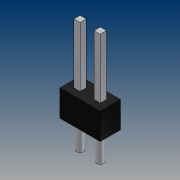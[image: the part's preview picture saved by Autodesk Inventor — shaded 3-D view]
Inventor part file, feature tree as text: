
AUTODESK INVENTOR PART (.ipt)
format: ipt  version: 2012 (Build 160160000, 160)  size: 101,376 bytes
history: native  units: mm (DEFAULTED — no unit token found)
features: extrude x3, plane x3, sketch x2, pattern_linear x1
ambient origin geometry x5: Origin, X Axis, Y Axis, Z Axis, Center Point
bodies: Solid1 (feature_tree)
feature tree (9):
  extrude  "Extrusion1"  Depth=3.302mm
  sketch  "Sketch3"  dims[d2=2.54mm d3=0.0mm d4=0.762mm d5=0.889mm d6=10.795mm d7=0.0mm d8=3.429mm d9=0.0mm d10=20.0mm d12=2.54mm]
  extrude  "Extrusion2"  Depth=0.762mm
  extrude  "Extrusion3"  Depth=0.889mm
  pattern_linear  "Rectangular Pattern1"  Spacing1=10.795mm  [1 undecoded]
  plane  "YZ Plane (RIGHT)"
  plane  "XZ Plane (TOP)"
  plane  "XY Plane (FRONT)"
  sketch  "Sketch2"  dims[d0=2.54mm d1=3.302mm]
note: 1 required parameter value undecoded (feature->parameter linkage not recoverable at this tier; creation-order binding heuristic only, values carry confidence <= 0.55)
